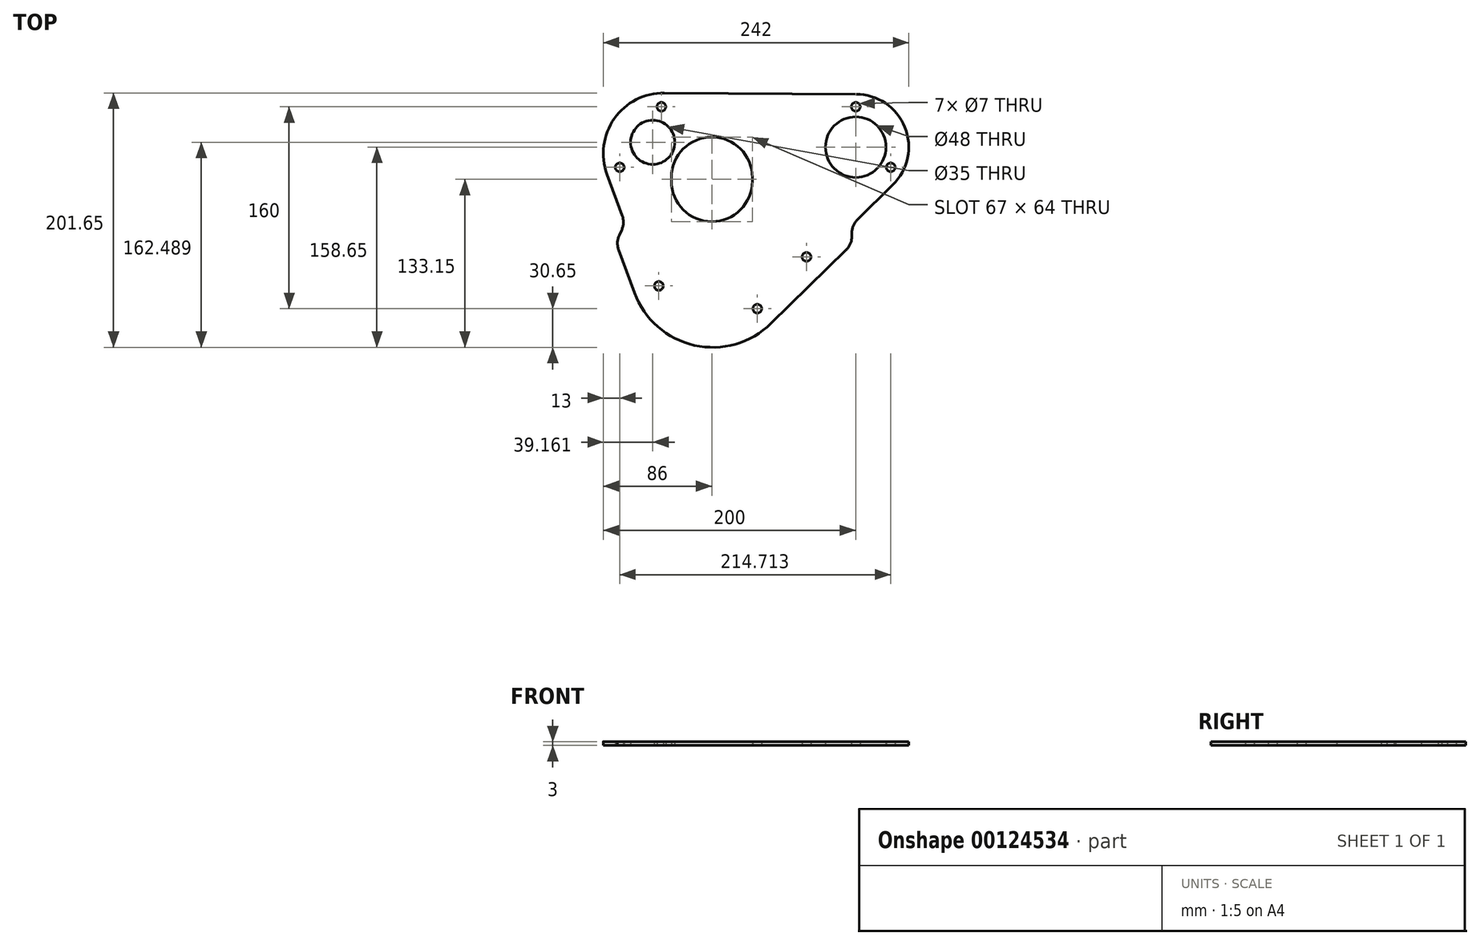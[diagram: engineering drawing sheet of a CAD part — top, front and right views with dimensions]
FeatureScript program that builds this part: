
annotation { "Feature Type Name" : "Feature", "Feature Type Description" : "" }
export const myFeature = defineFeature(function(context is Context, id is Id, definition is map)
    precondition{}
    {
        {
            var Q0;
            Q0=qCreatedBy(makeId("Top.planeOp"),FACE);
            var sketch = newSketch(context, id + "F0", { "sketchPlane" : qUnion([Q0])});
            skCircle(sketch, "E0", {"center": v(0, 0) * mm, "radius": 3.5 * mm});
            skCircle(sketch, "E1", {"center": v(154, 0) * mm, "radius": 3.5 * mm});
            skCircle(sketch, "E2", {"center": v(-33, -48) * mm, "radius": 3.5 * mm});
            skCircle(sketch, "E3", {"center": v(-2, -142) * mm, "radius": 3.5 * mm});
            skCircle(sketch, "E4", {"center": v(76, -160) * mm, "radius": 3.5 * mm});
            skCircle(sketch, "E5", {"center": v(115, -119) * mm, "radius": 3.5 * mm});
            skCircle(sketch, "E6", {"center": v(181.71, -48) * mm, "radius": 3.5 * mm});
            skArc(sketch, "E7", {"start": v(72, -56) * mm, "mid": v(40, -24) * mm, "end": v(8, -56) * mm});
            skArc(sketch, "E8", {"start": v(8, -59) * mm, "mid": v(40, -91) * mm, "end": v(72, -59) * mm});
            skLineSegment(sketch, "E9", {"start": v(72, -59) * mm, "end": v(72, -56) * mm});
            skLineSegment(sketch, "E10", {"start": v(8, -59) * mm, "end": v(8, -56) * mm});
            skCircle(sketch, "E11", {"center": v(154, -32) * mm, "radius": 24 * mm});
            skLineSegment(sketch, "E12", {"start": v(154, -32) * mm, "end": v(181.71, -48) * mm, "construction": true});
            skLineSegment(sketch, "E13", {"start": v(154, -32) * mm, "end": v(154, 0) * mm, "construction": true});
            skLineSegment(sketch, "E14", {"start": v(126.29, -48) * mm, "end": v(154, -32) * mm, "construction": true});
            skPoint(sketch, "E15", {"position": v(2, -37) * mm});
            skArc(sketch, "E16", {"start": v(2.32, 11) * mm, "mid": v(-37.28, -9.4) * mm, "end": v(-43.05, -53.57) * mm});
            skArc(sketch, "E17", {"start": v(183.39, -62) * mm, "mid": v(192.94, -16.26) * mm, "end": v(154.28, 10) * mm});
            skLineSegment(sketch, "E18", {"start": v(86.82, -171.8) * mm, "end": v(146.4, -113.43) * mm});
            skLineSegment(sketch, "E19", {"start": v(155.44, -89.38) * mm, "end": v(183.39, -62) * mm});
            skLineSegment(sketch, "E20", {"start": v(-43.05, -53.57) * mm, "end": v(-31.01, -86.3) * mm});
            skLineSegment(sketch, "E21", {"start": v(-33.84, -113.36) * mm, "end": v(-21.31, -147.44) * mm});
            skLineSegment(sketch, "E22", {"start": v(2.32, 11) * mm, "end": v(154.28, 10) * mm});
            skLineSegment(sketch, "E23", {"start": v(-33.38, -101.9) * mm, "end": v(-31.47, -97.77) * mm});
            skPoint(sketch, "E24", {"position": v(-32.43, -99.83) * mm});
            skLineSegment(sketch, "E25", {"start": v(150.9, -102.87) * mm, "end": v(150.94, -99.94) * mm});
            skPoint(sketch, "E26", {"position": v(150.92, -101.4) * mm});
            skLineSegment(sketch, "E27.trimOffspring", {"start": v(5.69, -186.07) * mm, "end": v(5.73, -186.2) * mm});
            skPoint(sketch, "E28.visualSharp", {"position": v(-28.87, -92.13) * mm});
            skArc(sketch, "E28.filletArc", {"start": v(-31.47, -97.77) * mm, "mid": v(-30.1, -92.08) * mm, "end": v(-31.01, -86.3) * mm});
            skPoint(sketch, "E29.visualSharp", {"position": v(-35.99, -107.53) * mm});
            skArc(sketch, "E29.filletArc", {"start": v(-33.38, -101.9) * mm, "mid": v(-34.75, -107.58) * mm, "end": v(-33.84, -113.36) * mm});
            skPoint(sketch, "E30.visualSharp", {"position": v(151, -93.73) * mm});
            skArc(sketch, "E30.filletArc", {"start": v(155.44, -89.38) * mm, "mid": v(152.14, -94.21) * mm, "end": v(150.94, -99.94) * mm});
            skPoint(sketch, "E31.visualSharp", {"position": v(150.84, -109.09) * mm});
            skArc(sketch, "E31.filletArc", {"start": v(146.4, -113.43) * mm, "mid": v(149.7, -108.6) * mm, "end": v(150.9, -102.87) * mm});
            skCircle(sketch, "E32", {"center": v(2, -37) * mm, "radius": 30 * mm, "construction": true});
            skCircle(sketch, "E33", {"center": v(-6.84, -28.16) * mm, "radius": 17.5 * mm});
            skCircle(sketch, "E34", {"center": v(40, -56) * mm, "radius": 37 * mm, "construction": true});
            skLineSegment(sketch, "E35", {"start": v(2, -37) * mm, "end": v(-51.88, 16.88) * mm, "construction": true});
            skLineSegment(sketch, "E36", {"start": v(-24.37, -190.65) * mm, "end": v(100.5, -190.65) * mm, "construction": true});
            skArc(sketch, "E37", {"start": v(-21.31, -147.44) * mm, "mid": v(26.12, -189.04) * mm, "end": v(86.82, -171.8) * mm});
            skSolve(sketch);
        }
        {
            var Q0;
            Q0 = qSketchRegion(id + "F0", true);
            extrude(context, id + "F1", {"entities" : qUnion([Q0]), "depth" : 3 * mm});
        }
    });
